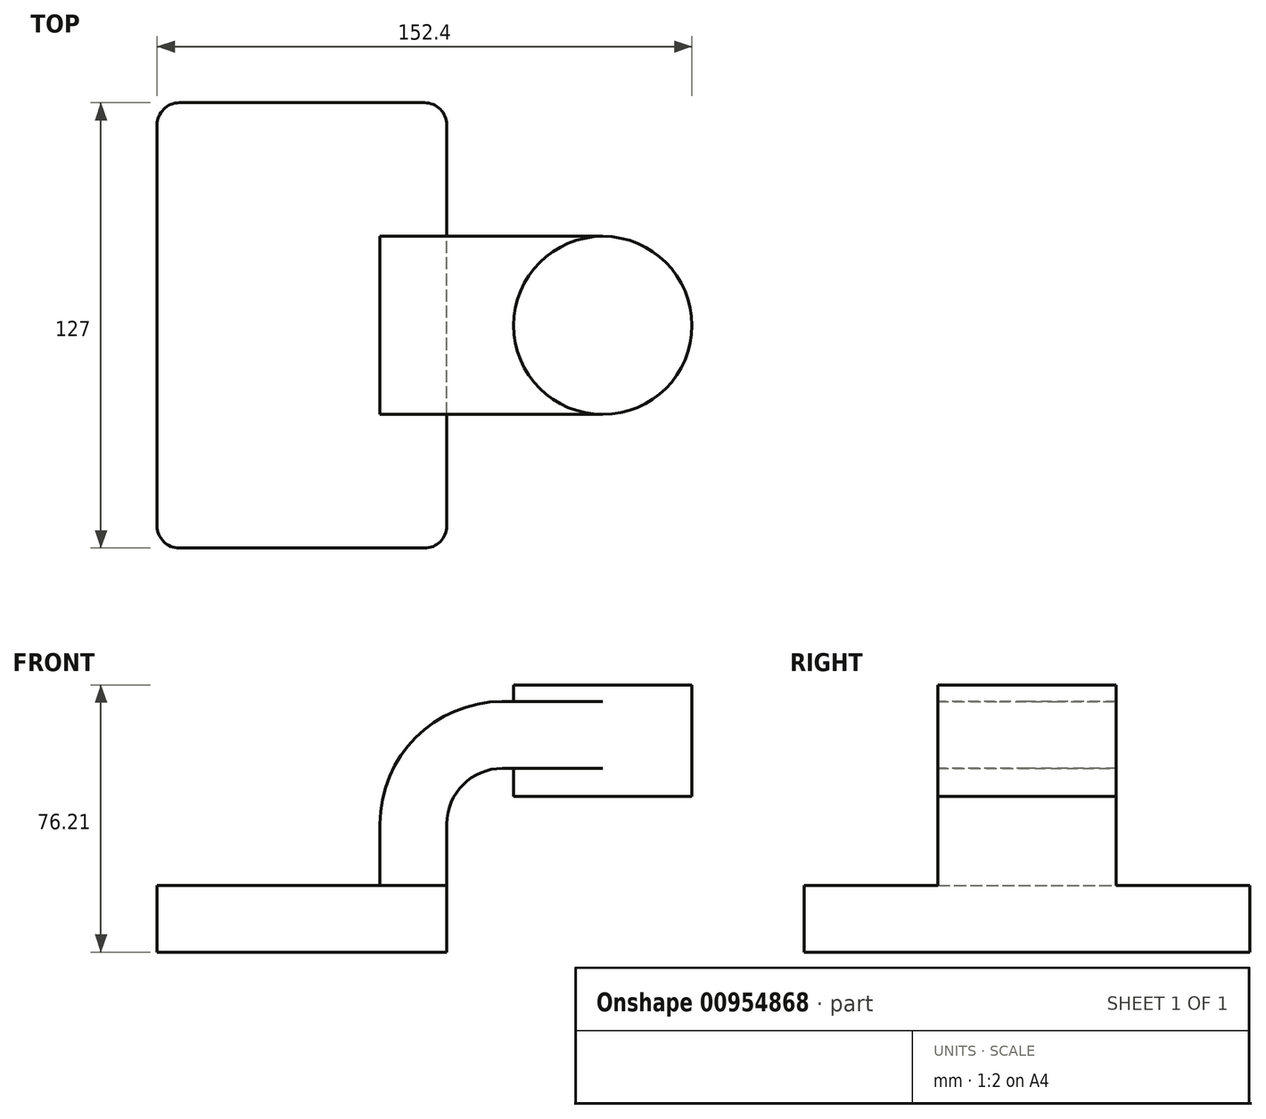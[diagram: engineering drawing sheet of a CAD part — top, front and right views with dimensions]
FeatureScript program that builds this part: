
annotation { "Feature Type Name" : "Feature", "Feature Type Description" : "" }
export const myFeature = defineFeature(function(context is Context, id is Id, definition is map)
    precondition{}
    {
        {
            var Q0;
            Q0=qCreatedBy(makeId("Front.planeOp"),FACE);
            var sketch = newSketch(context, id + "F0", { "sketchPlane" : qUnion([Q0])});
            skLineSegment(sketch, "E0.bottom", {"start": v(-41.28, 9.52) * mm, "end": v(41.28, 9.53) * mm});
            skLineSegment(sketch, "E0.top", {"start": v(-41.28, -9.53) * mm, "end": v(41.28, -9.53) * mm});
            skLineSegment(sketch, "E0.left", {"start": v(-41.28, 9.52) * mm, "end": v(-41.27, -9.53) * mm});
            skLineSegment(sketch, "E0.right", {"start": v(41.28, 9.53) * mm, "end": v(41.28, -9.52) * mm});
            skPoint(sketch, "E0.middle", {"position": v(0, 0) * mm});
            skLineSegment(sketch, "E1.bottom", {"start": v(60.33, 34.93) * mm, "end": v(111.12, 34.93) * mm});
            skLineSegment(sketch, "E1.top", {"start": v(60.32, 66.67) * mm, "end": v(111.12, 66.67) * mm});
            skLineSegment(sketch, "E1.left", {"start": v(60.33, 34.93) * mm, "end": v(60.32, 66.67) * mm});
            skLineSegment(sketch, "E1.right", {"start": v(111.12, 34.93) * mm, "end": v(111.12, 66.67) * mm});
            skPoint(sketch, "E1.middle", {"position": v(85.72, 50.8) * mm});
            skLineSegment(sketch, "E2", {"start": v(41.27, 9.53) * mm, "end": v(41.27, 27) * mm});
            skArc(sketch, "E3", {"start": v(41.27, 27) * mm, "mid": v(45.92, 38.23) * mm, "end": v(57.15, 42.88) * mm});
            skLineSegment(sketch, "E4", {"start": v(57.15, 42.88) * mm, "end": v(85.72, 42.88) * mm});
            skLineSegment(sketch, "E5.0", {"start": v(57.15, 61.93) * mm, "end": v(85.72, 61.93) * mm});
            skArc(sketch, "E5.1", {"start": v(22.23, 27) * mm, "mid": v(32.45, 51.7) * mm, "end": v(57.15, 61.93) * mm});
            skLineSegment(sketch, "E5.2", {"start": v(22.22, 9.53) * mm, "end": v(22.22, 27) * mm});
            skLineSegment(sketch, "E6", {"start": v(85.72, 34.93) * mm, "end": v(85.72, 66.67) * mm});
            skFitSpline(sketch, "E7", {"points": [v(-41.28, 9.52) * mm, v(57.15, 61.93) * mm], "startDerivative": vector(1.76, 90.62) * mm, "endDerivative": vector(127.42, 0.14) * mm});
            skSolve(sketch);
        }
        {
            var Q0;
            Q0=makeQuery(id+"F0.imprint","IMPRINT",FACE,{"disambiguationData":[TD([[makeQuery(id+"F0.imprint","IMPRINT",EDGE,{"derivedFrom":sQuery(id+"F0.wireOp",EDGE,"E0.top")}),1.0]])]});
            extrude(context, id + "F1", {"entities" : qUnion([Q0]), "depth" : 127 * mm, "offsetDistance" : 25.4 * mm, "symmetric" : true});
        }
        {
            var Q0;
            {var subQ5=sQuery(id+"F0.wireOp",EDGE,"E2");Q0=makeQuery(id+"F0.imprint","IMPRINT",FACE,{"disambiguationData":[TD([[makeQuery(id+"F0.imprint","IMPRINT",EDGE,{"derivedFrom":subQ5}),1.0]])]});}
            var Q1;
            {var subQ0=sQuery(id+"F0.wireOp",EDGE,"E4");var subQ1=sQuery(id+"F0.wireOp",EDGE,"E1.left");var subQ2=makeQuery(id+"F0.imprint","INTERSECT",VERTEX,{"derivedFrom":[subQ1,subQ0]});Q1=makeQuery(id+"F0.imprint","IMPRINT",FACE,{"disambiguationData":[TD([[makeQuery(id+"F0.imprint","IMPRINT",EDGE,{"disambiguationData":[TD([[subQ2,-1.0]])],"derivedFrom":subQ1}),-1.0]])]});}
            extrude(context, id + "F2", {"entities" : qUnion([Q0, Q1]), "operationType" : NewBodyOperationType.ADD, "depth" : 50.8 * mm, "offsetDistance" : 25.4 * mm, "symmetric" : true});
        }
        {
            var Q0;
            {var subQ4=sQuery(id+"F0.wireOp",EDGE,"E5.1");Q0=makeQuery(id+"F0.imprint","IMPRINT",FACE,{"disambiguationData":[TD([[makeQuery(id+"F0.imprint","IMPRINT",EDGE,{"derivedFrom":subQ4}),1.0]])]});}
            extrude(context, id + "F3", {"entities" : qUnion([Q0]), "operationType" : NewBodyOperationType.ADD, "depth" : 15.88 * mm, "offsetDistance" : 25.4 * mm, "symmetric" : true});
        }
        {
            var Q0;
            {var subQ0=sQuery(id+"F0.wireOp",EDGE,"E1.right");Q0=makeQuery(id+"F0.imprint","IMPRINT",FACE,{"disambiguationData":[TD([[makeQuery(id+"F0.imprint","IMPRINT",EDGE,{"derivedFrom":subQ0}),1.0]])]});}
            var Q1;
            Q1=sQuery(id+"F0.wireOp",EDGE,"E6");
            revolve(context, id + "F4", {"operationType" : NewBodyOperationType.ADD, "surfaceOperationType" : NewSurfaceOperationType.NEW, "entities" : qUnion([Q0]), "axis" : qUnion([Q1]), "revolveType" : RevolveType.FULL});
        }
        {
            var Q0;
            Q0=makeQuery(id+"F1.opExtrude","CAP_EDGE",EDGE,{"disambiguationData":[OSD([sQuery(id+"F0.wireOp",EDGE,"E0.right")])],"isStart":false});
            var Q1;
            Q1=makeQuery(id+"F1.opExtrude","CAP_EDGE",EDGE,{"disambiguationData":[OSD([sQuery(id+"F0.wireOp",EDGE,"E0.left")])],"isStart":false});
            var Q2;
            Q2=makeQuery(id+"F1.opExtrude","CAP_EDGE",EDGE,{"disambiguationData":[OSD([sQuery(id+"F0.wireOp",EDGE,"E0.left")])],"isStart":true});
            var Q3;
            Q3=makeQuery(id+"F1.opExtrude","CAP_EDGE",EDGE,{"disambiguationData":[OSD([sQuery(id+"F0.wireOp",EDGE,"E0.right")])],"isStart":true});
            fillet(context, id + "F5", {"entities" : qUnion([Q0, Q1, Q2, Q3]), "radius" : 6.35 * mm, "tangentPropagation" : true, "allowEdgeOverflow" : false});
        }
    });
